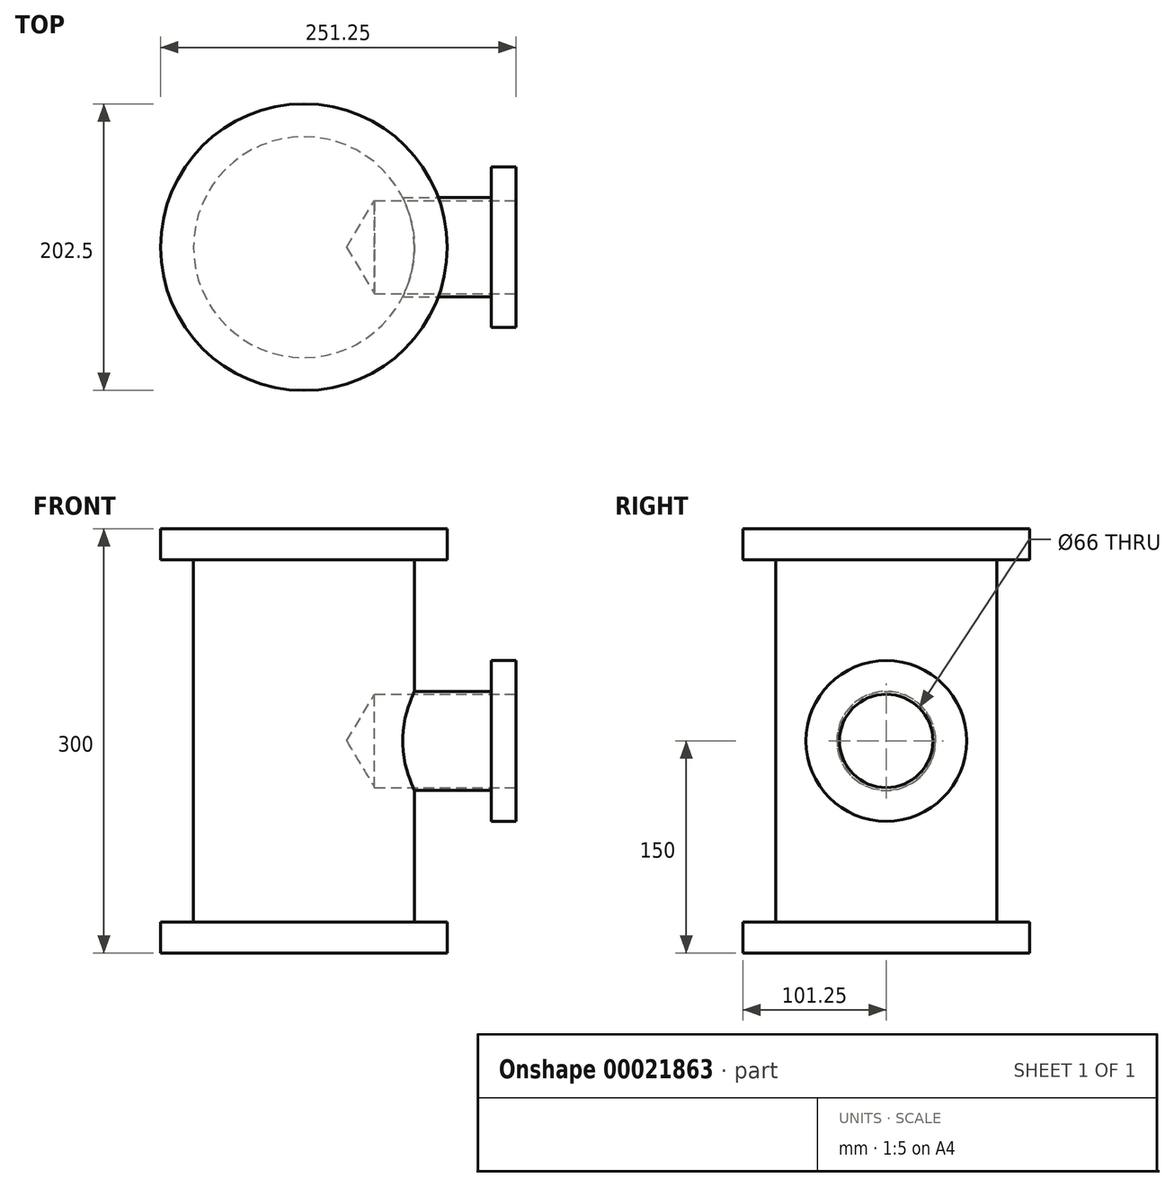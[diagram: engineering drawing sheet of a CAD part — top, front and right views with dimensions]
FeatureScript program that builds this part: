
annotation { "Feature Type Name" : "Feature", "Feature Type Description" : "" }
export const myFeature = defineFeature(function(context is Context, id is Id, definition is map)
    precondition{}
    {
        {
            var Q0;
            Q0=qCreatedBy(makeId("Front.planeOp"),FACE);
            var sketch = newSketch(context, id + "F0", { "sketchPlane" : qUnion([Q0])});
            skLineSegment(sketch, "E0", {"start": v(0, 0) * mm, "end": v(0, 150) * mm, "construction": true});
            skLineSegment(sketch, "E1", {"start": v(0, 150) * mm, "end": v(101.25, 150) * mm});
            skLineSegment(sketch, "E2", {"start": v(101.25, 150) * mm, "end": v(101.25, 128) * mm});
            skLineSegment(sketch, "E3", {"start": v(101.25, 128) * mm, "end": v(78, 128) * mm});
            skLineSegment(sketch, "E4", {"start": v(78, 128) * mm, "end": v(78, -128) * mm});
            skLineSegment(sketch, "E5", {"start": v(78, -128) * mm, "end": v(101.25, -128) * mm});
            skLineSegment(sketch, "E6", {"start": v(101.25, -128) * mm, "end": v(101.25, -150) * mm});
            skLineSegment(sketch, "E7", {"start": v(101.25, -150) * mm, "end": v(0, -150) * mm});
            skLineSegment(sketch, "E8", {"start": v(0, -150) * mm, "end": v(0, 150) * mm});
            skSolve(sketch);
        }
        {
            var Q0;
            Q0=makeQuery(id+"F0.imprint","IMPRINT",FACE,{"disambiguationData":[TD([[makeQuery(id+"F0.imprint","IMPRINT",EDGE,{"derivedFrom":sQuery(id+"F0.wireOp",EDGE,"E1")}),-1.0]])]});
            var Q1;
            Q1=sQuery(id+"F0.wireOp",EDGE,"E0");
            revolve(context, id + "F1", {"entities" : qUnion([Q0]), "axis" : qUnion([Q1]), "revolveType" : RevolveType.FULL});
        }
        {
            var Q0;
            Q0=qCreatedBy(makeId("Front.planeOp"),FACE);
            var sketch = newSketch(context, id + "F2", { "sketchPlane" : qUnion([Q0])});
            skLineSegment(sketch, "E9", {"start": v(0, 0) * mm, "end": v(0, 35) * mm});
            skLineSegment(sketch, "E10", {"start": v(0, 35) * mm, "end": v(132.5, 35) * mm});
            skLineSegment(sketch, "E11", {"start": v(132.5, 35) * mm, "end": v(132.5, 56.75) * mm});
            skLineSegment(sketch, "E12", {"start": v(132.5, 56.75) * mm, "end": v(150, 56.75) * mm});
            skLineSegment(sketch, "E13", {"start": v(150, 56.75) * mm, "end": v(150, 0) * mm});
            skLineSegment(sketch, "E14", {"start": v(150, 0) * mm, "end": v(0, 0) * mm});
            skSolve(sketch);
        }
        {
            var Q0;
            Q0=makeQuery(id+"F2.imprint","IMPRINT",FACE,{"disambiguationData":[TD([[makeQuery(id+"F2.imprint","IMPRINT",EDGE,{"derivedFrom":sQuery(id+"F2.wireOp",EDGE,"E9")}),-1.0]])]});
            var Q1;
            Q1=sQuery(id+"F2.wireOp",EDGE,"E14");
            revolve(context, id + "F3", {"operationType" : NewBodyOperationType.ADD, "entities" : qUnion([Q0]), "axis" : qUnion([Q1]), "revolveType" : RevolveType.FULL});
        }
        {
            var Q0;
            Q0=makeQuery(id+"F3.opRevolve","SWEPT_FACE",FACE,{"disambiguationData":[OSD([sQuery(id+"F2.wireOp",EDGE,"E13")])]});
            var sketch = newSketch(context, id + "F4", { "sketchPlane" : qUnion([Q0])});
            skPoint(sketch, "E15", {"position": v(0, 0) * mm});
            skSolve(sketch);
        }
        {
            var Q0;
            Q0=sQuery(id+"F4.wireOp",VERTEX,"E15");
            var Q1;
            Q1=makeQuery(id+"F1.opRevolve","SWEPT_BODY",BODY,{"disambiguationData":[OSD([sQuery(id+"F0.wireOp",EDGE,"E1"),sQuery(id+"F0.wireOp",EDGE,"E2"),sQuery(id+"F0.wireOp",EDGE,"E3"),sQuery(id+"F0.wireOp",EDGE,"E4"),sQuery(id+"F0.wireOp",EDGE,"E5"),sQuery(id+"F0.wireOp",EDGE,"E6"),sQuery(id+"F0.wireOp",EDGE,"E7"),sQuery(id+"F0.wireOp",EDGE,"E8")])]});
            hole(context, id + "F5", {"style" : HoleStyle.SIMPLE, "holeDiameter" : 66 * mm, "endStyle" : HoleEndStyle.BLIND, "holeDepth" : 100 * mm, "locations" : qUnion([Q0]), "scope" : qUnion([Q1])});
        }
    });
